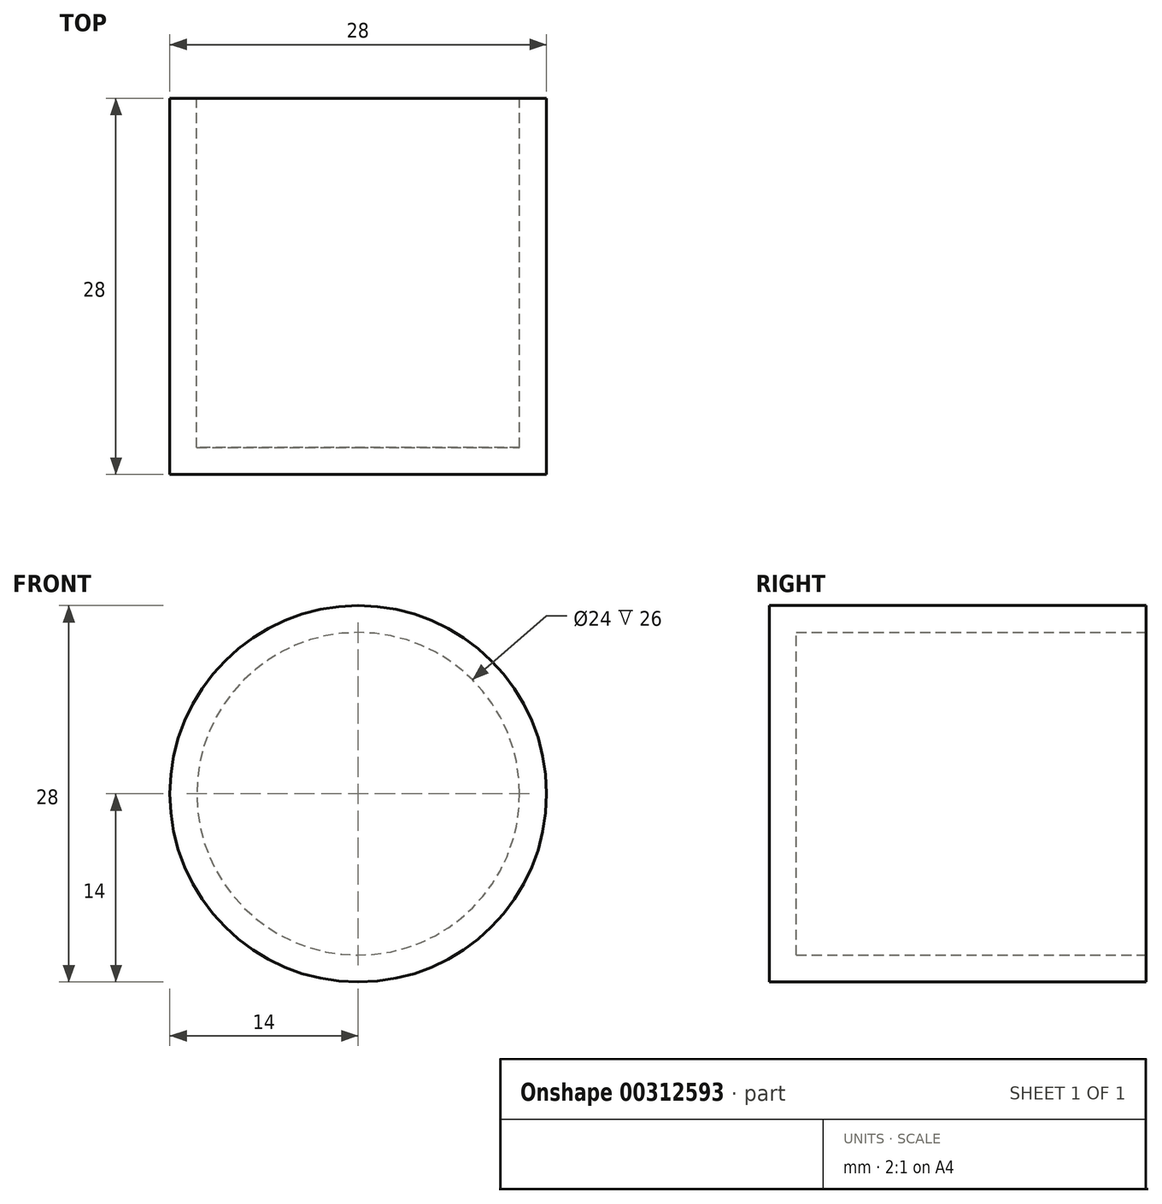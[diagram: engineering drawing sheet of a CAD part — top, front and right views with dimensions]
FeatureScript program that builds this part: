
annotation { "Feature Type Name" : "Feature", "Feature Type Description" : "" }
export const myFeature = defineFeature(function(context is Context, id is Id, definition is map)
    precondition{}
    {
        {
            var Q0;
            Q0=qCreatedBy(makeId("Front.planeOp"),FACE);
            var sketch = newSketch(context, id + "F0", { "sketchPlane" : qUnion([Q0])});
            skCircle(sketch, "E0", {"center": v(0, 0) * mm, "radius": 12 * mm});
            skCircle(sketch, "E1.0", {"center": v(0, 0) * mm, "radius": 14 * mm});
            skSolve(sketch);
        }
        {
            var Q0;
            Q0=makeQuery(id+"F0.imprint","IMPRINT",FACE,{"disambiguationData":[TD([[makeQuery(id+"F0.imprint","IMPRINT",EDGE,{"derivedFrom":sQuery(id+"F0.wireOp",EDGE,"E0")}),-1.0]])]});
            extrude(context, id + "F1", {"entities" : qUnion([Q0]), "depth" : 28 * mm});
        }
        {
            var Q0;
            Q0=makeQuery(id+"F1.opExtrude","CAP_FACE",FACE,{"disambiguationData":[OSD([sQuery(id+"F0.wireOp",EDGE,"E0"),sQuery(id+"F0.wireOp",EDGE,"E1.0")])],"isStart":false});
            var sketch = newSketch(context, id + "F2", { "sketchPlane" : qUnion([Q0])});
            skCircle(sketch, "E2.0", {"center": v(0, 0) * mm, "radius": 14 * mm});
            skSolve(sketch);
        }
        {
            var Q0;
            Q0 = qSketchRegion(id + "F2", true);
            extrude(context, id + "F3", {"entities" : qUnion([Q0]), "operationType" : NewBodyOperationType.ADD, "oppositeDirection" : true, "depth" : 2 * mm});
        }
    });
